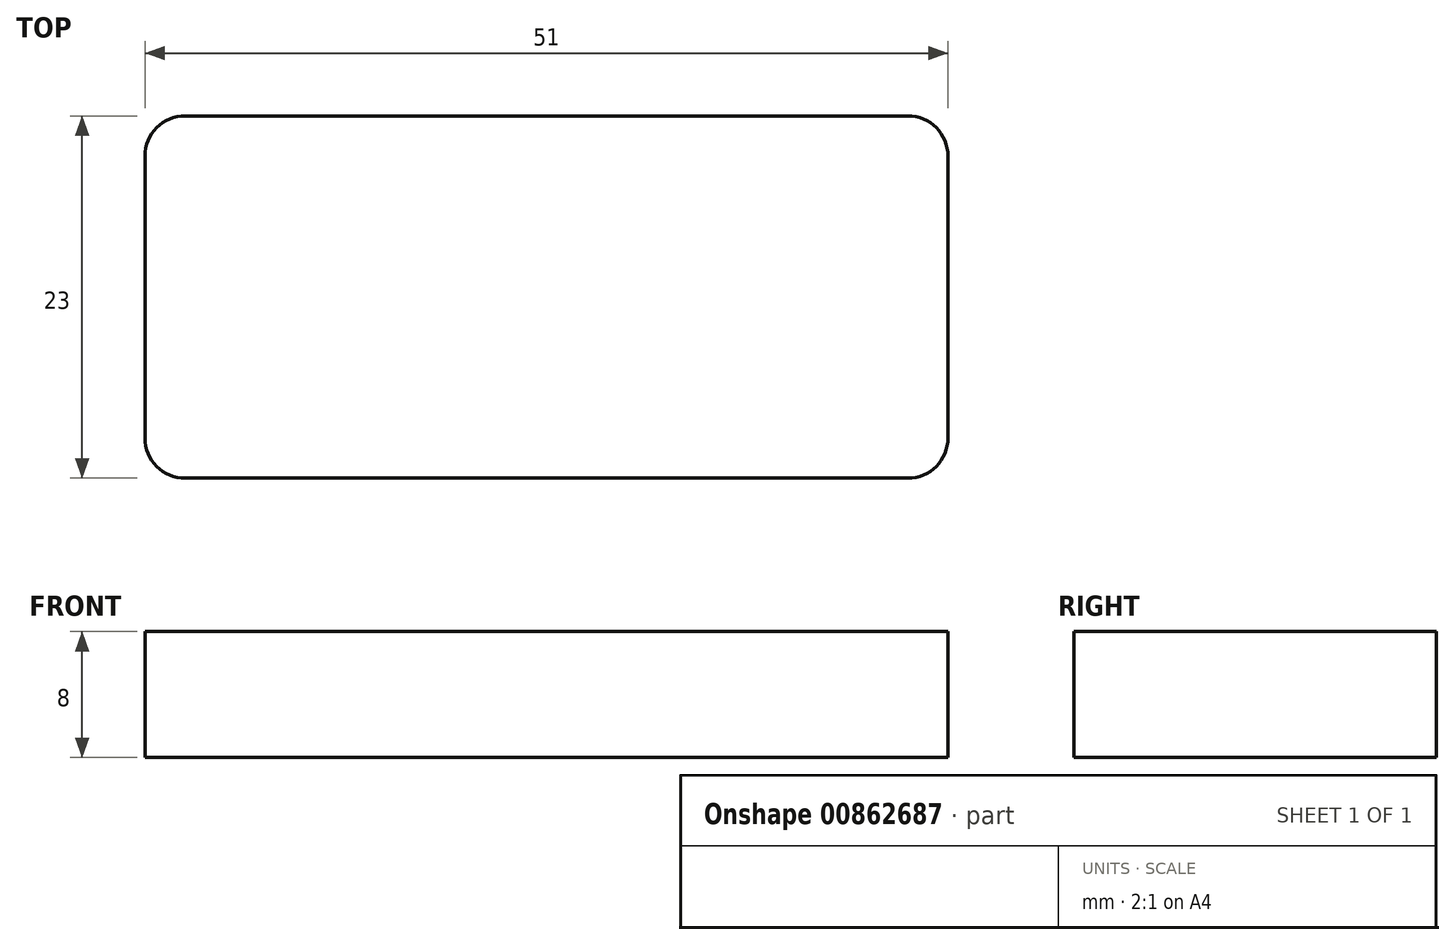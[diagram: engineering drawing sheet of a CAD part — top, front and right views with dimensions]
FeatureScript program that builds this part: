
annotation { "Feature Type Name" : "Feature", "Feature Type Description" : "" }
export const myFeature = defineFeature(function(context is Context, id is Id, definition is map)
    precondition{}
    {
        {
            var Q0;
            Q0=qCreatedBy(makeId("Top.planeOp"),FACE);
            var sketch = newSketch(context, id + "F0", { "sketchPlane" : qUnion([Q0])});
            skLineSegment(sketch, "E0.bottom", {"start": v(26.84, 11.5) * mm, "end": v(-24.16, 11.5) * mm});
            skLineSegment(sketch, "E0.top", {"start": v(26.84, -11.5) * mm, "end": v(-24.16, -11.5) * mm});
            skLineSegment(sketch, "E0.left", {"start": v(26.84, 11.5) * mm, "end": v(26.84, -11.5) * mm});
            skLineSegment(sketch, "E0.right", {"start": v(-24.16, 11.5) * mm, "end": v(-24.16, -11.5) * mm});
            skPoint(sketch, "E0.middle", {"position": v(1.34, 0) * mm});
            skSolve(sketch);
        }
        {
            var Q0;
            Q0=makeQuery(id+"F0.imprint","IMPRINT",FACE,{"disambiguationData":[TD([[makeQuery(id+"F0.imprint","IMPRINT",EDGE,{"derivedFrom":sQuery(id+"F0.wireOp",EDGE,"E0.bottom")}),1.0]])]});
            extrude(context, id + "F1", {"entities" : qUnion([Q0]), "depth" : 8 * mm, "offsetDistance" : 25.4 * mm});
        }
        {
            var Q0;
            Q0=makeQuery(id+"F1.opExtrude","SWEPT_EDGE",EDGE,{"disambiguationData":[OSD([sQuery(id+"F0.wireOp",EDGE,"E0.bottom"),sQuery(id+"F0.wireOp",EDGE,"E0.right")])]});
            var Q1;
            Q1=makeQuery(id+"F1.opExtrude","SWEPT_EDGE",EDGE,{"disambiguationData":[OSD([sQuery(id+"F0.wireOp",EDGE,"E0.top"),sQuery(id+"F0.wireOp",EDGE,"E0.right")])]});
            var Q2;
            Q2=makeQuery(id+"F1.opExtrude","SWEPT_EDGE",EDGE,{"disambiguationData":[OSD([sQuery(id+"F0.wireOp",EDGE,"E0.bottom"),sQuery(id+"F0.wireOp",EDGE,"E0.left")])]});
            var Q3;
            Q3=makeQuery(id+"F1.opExtrude","SWEPT_EDGE",EDGE,{"disambiguationData":[OSD([sQuery(id+"F0.wireOp",EDGE,"E0.top"),sQuery(id+"F0.wireOp",EDGE,"E0.left")])]});
            fillet(context, id + "F2", {"entities" : qUnion([Q0, Q1, Q2, Q3]), "radius" : 2.54 * mm, "tangentPropagation" : true, "allowEdgeOverflow" : false});
        }
    });
